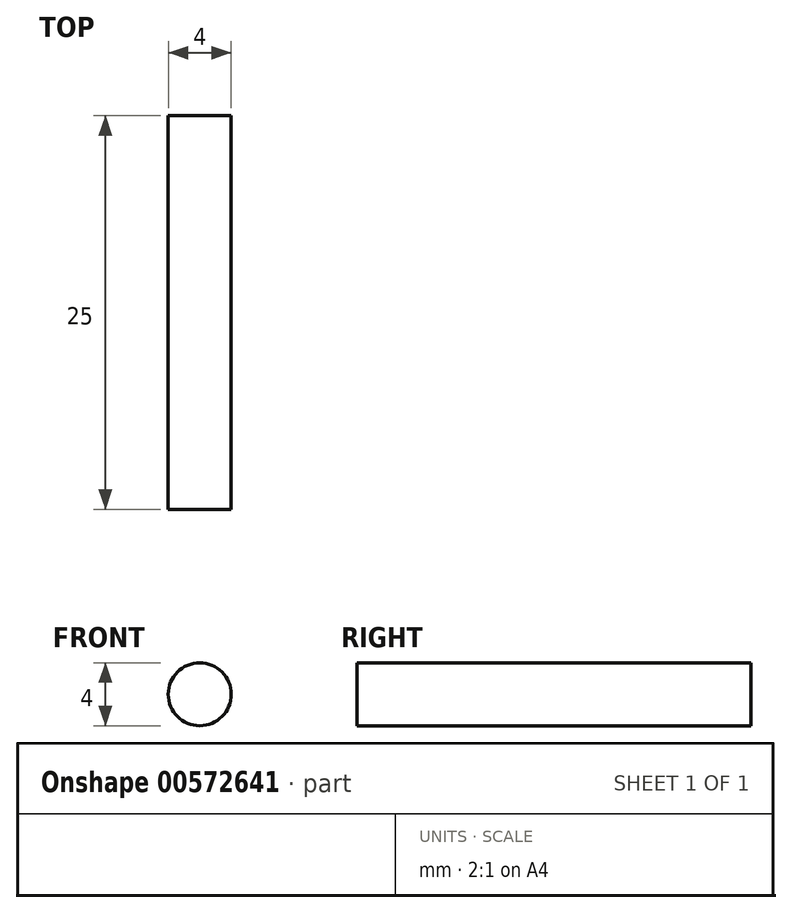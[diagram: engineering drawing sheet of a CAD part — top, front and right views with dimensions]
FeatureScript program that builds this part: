
annotation { "Feature Type Name" : "Feature", "Feature Type Description" : "" }
export const myFeature = defineFeature(function(context is Context, id is Id, definition is map)
    precondition{}
    {
        {
            var Q0;
            Q0=qCreatedBy(makeId("Front.planeOp"),FACE);
            var sketch = newSketch(context, id + "F0", { "sketchPlane" : qUnion([Q0])});
            skCircle(sketch, "E0", {"center": v(-16.02, -6.96) * mm, "radius": 2 * mm});
            skSolve(sketch);
        }
        {
            var Q0;
            Q0 = qSketchRegion(id + "F0", true);
            extrude(context, id + "F1", {"entities" : qUnion([Q0]), "depth" : 25 * mm, "offsetDistance" : 25 * mm});
        }
    });
